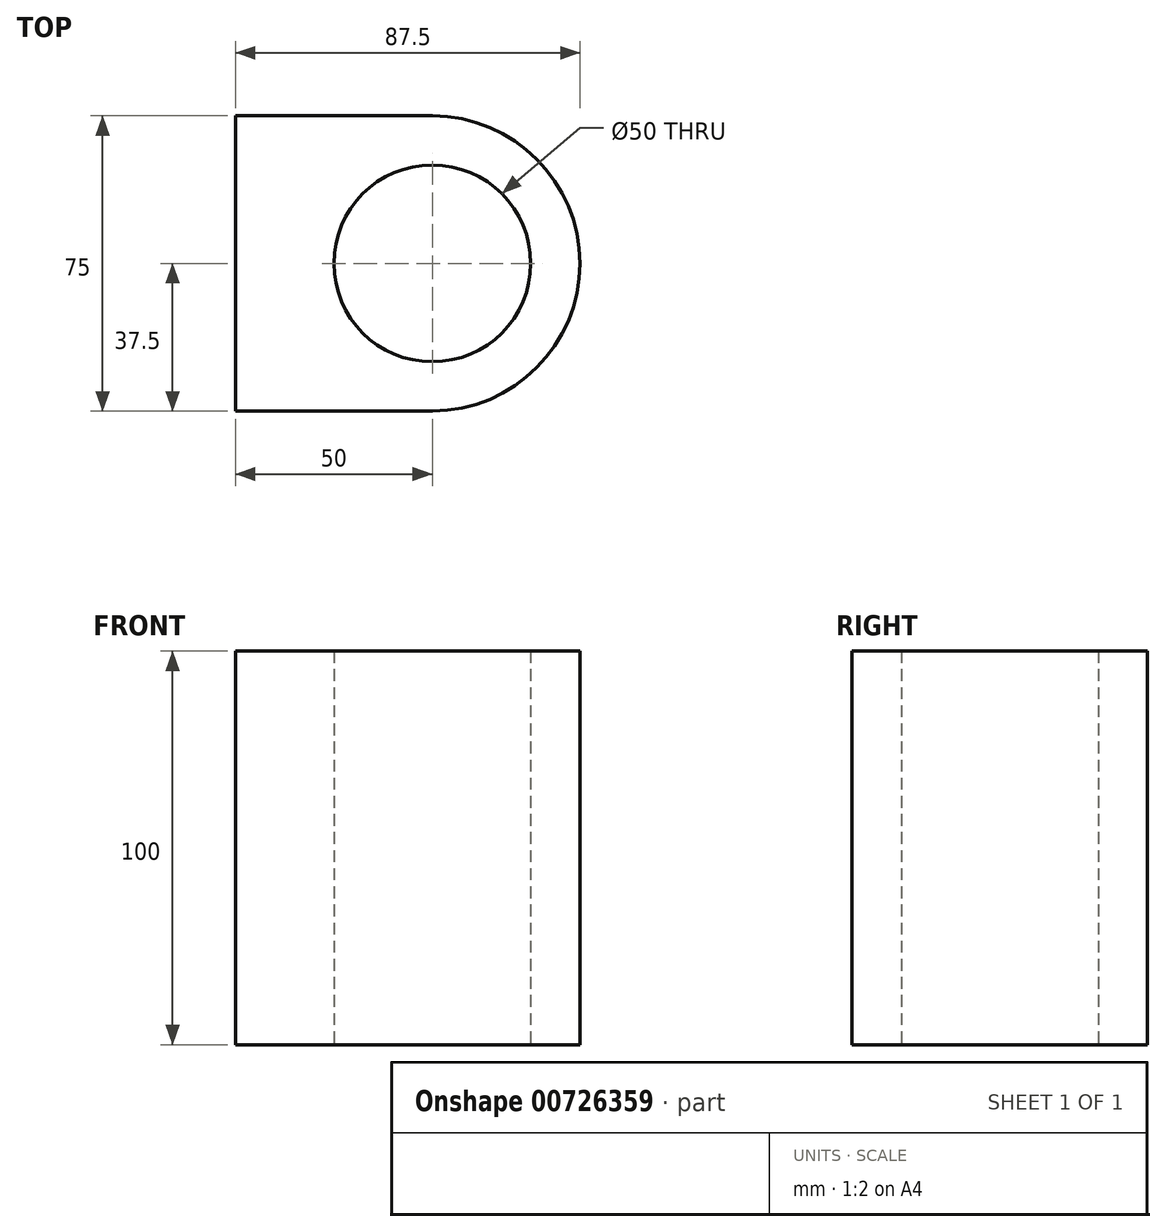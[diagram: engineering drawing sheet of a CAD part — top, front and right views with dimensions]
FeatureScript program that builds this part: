
annotation { "Feature Type Name" : "Feature", "Feature Type Description" : "" }
export const myFeature = defineFeature(function(context is Context, id is Id, definition is map)
    precondition{}
    {
        {
            var Q0;
            Q0=qCreatedBy(makeId("Top.planeOp"),FACE);
            var sketch = newSketch(context, id + "F0", { "sketchPlane" : qUnion([Q0])});
            skLineSegment(sketch, "E0.bottom", {"start": v(0, 0) * mm, "end": v(50, 0) * mm});
            skLineSegment(sketch, "E0.top", {"start": v(0, 75) * mm, "end": v(50, 75) * mm});
            skLineSegment(sketch, "E0.left", {"start": v(0, 0) * mm, "end": v(0, 75) * mm});
            skLineSegment(sketch, "E0.right", {"start": v(50, 0) * mm, "end": v(50, 75) * mm});
            skCircle(sketch, "E1", {"center": v(50, 37.5) * mm, "radius": 25 * mm});
            skArc(sketch, "E2", {"start": v(50, 0) * mm, "mid": v(87.5, 37.5) * mm, "end": v(50, 75) * mm});
            skSolve(sketch);
        }
        {
            var Q0;
            Q0 = qSketchRegion(id + "F0", true);
            extrude(context, id + "F1", {"entities" : qUnion([Q0]), "depth" : 100 * mm, "offsetDistance" : 25 * mm});
        }
    });
